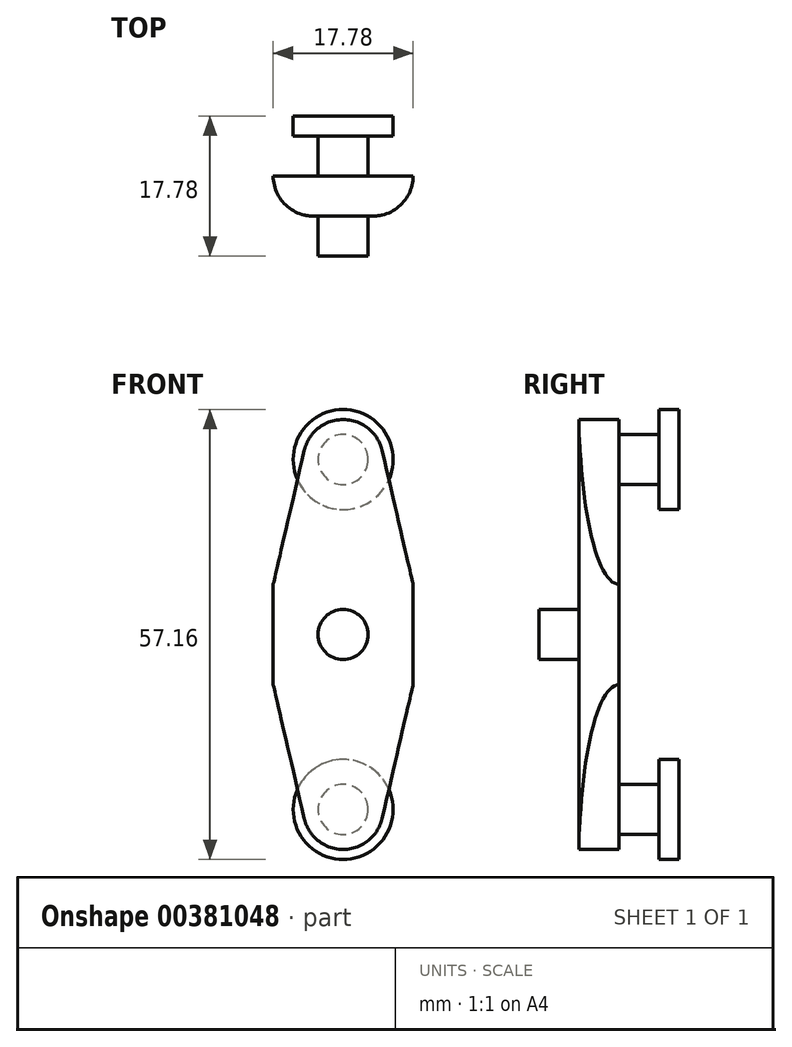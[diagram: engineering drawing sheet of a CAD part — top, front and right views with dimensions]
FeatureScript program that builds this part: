
annotation { "Feature Type Name" : "Feature", "Feature Type Description" : "" }
export const myFeature = defineFeature(function(context is Context, id is Id, definition is map)
    precondition{}
    {
        {
            var Q0;
            Q0=qCreatedBy(makeId("Front.planeOp"),FACE);
            var sketch = newSketch(context, id + "F0", { "sketchPlane" : qUnion([Q0])});
            skCircle(sketch, "E0", {"center": v(0, 22.23) * mm, "radius": 6.35 * mm});
            skSolve(sketch);
        }
        {
            var Q0;
            Q0 = qSketchRegion(id + "F0", true);
            extrude(context, id + "F1", {"entities" : qUnion([Q0]), "depth" : 2.54 * mm});
        }
        {
            var Q0;
            Q0=makeQuery(id+"F1.opExtrude","CAP_FACE",FACE,{"disambiguationData":[OSD([sQuery(id+"F0.wireOp",EDGE,"E0")])],"isStart":false});
            var sketch = newSketch(context, id + "F2", { "sketchPlane" : qUnion([Q0])});
            skCircle(sketch, "E1", {"center": v(0, 22.23) * mm, "radius": 3.18 * mm});
            skSolve(sketch);
        }
        {
            var Q0;
            Q0=makeQuery(id+"F2.imprint","IMPRINT",FACE,{"disambiguationData":[TD([[makeQuery(id+"F2.imprint","IMPRINT",EDGE,{"derivedFrom":sQuery(id+"F2.wireOp",EDGE,"E1")}),1.0]])]});
            extrude(context, id + "F3", {"entities" : qUnion([Q0]), "operationType" : NewBodyOperationType.ADD, "depth" : 5.08 * mm});
        }
        {
            var Q0;
            Q0=makeQuery(id+"F3.opExtrude","CAP_FACE",FACE,{"disambiguationData":[OSD([sQuery(id+"F2.wireOp",EDGE,"E1")])],"isStart":false});
            var sketch = newSketch(context, id + "F4", { "sketchPlane" : qUnion([Q0])});
            skCircle(sketch, "E2", {"center": v(0, 22.23) * mm, "radius": 5.08 * mm});
            skLineSegment(sketch, "E3.bottom", {"start": v(8.9, 6.35) * mm, "end": v(-8.9, 6.35) * mm});
            skLineSegment(sketch, "E3.top", {"start": v(8.9, -6.35) * mm, "end": v(-8.9, -6.35) * mm});
            skLineSegment(sketch, "E3.left", {"start": v(8.9, 6.35) * mm, "end": v(8.9, -6.35) * mm});
            skLineSegment(sketch, "E3.right", {"start": v(-8.9, 6.35) * mm, "end": v(-8.9, -6.35) * mm});
            skPoint(sketch, "E3.middle", {"position": v(0, 0) * mm});
            skLineSegment(sketch, "E4", {"start": v(8.9, 6.35) * mm, "end": v(4.95, 23.37) * mm});
            skLineSegment(sketch, "E5", {"start": v(-4.95, 23.37) * mm, "end": v(-8.89, 6.35) * mm});
            skSolve(sketch);
        }
        {
            var Q0;
            Q0=makeQuery(id+"F4.imprint","IMPRINT",FACE,{"disambiguationData":[TD([[makeQuery(id+"F4.imprint","IMPRINT",EDGE,{"derivedFrom":sQuery(id+"F4.wireOp",EDGE,"E3.bottom")}),-1.0]])]});
            var Q1;
            Q1=makeQuery(id+"F4.imprint","IMPRINT",FACE,{"disambiguationData":[TD([[makeQuery(id+"F4.imprint","IMPRINT",EDGE,{"derivedFrom":makeQuery(id+"F3.opExtrude","CAP_EDGE",EDGE,{"disambiguationData":[OSD([sQuery(id+"F2.wireOp",EDGE,"E1")])],"isStart":false})}),-1.0]])]});
            var Q2;
            Q2=makeQuery(id+"F4.imprint","IMPRINT",FACE,{"disambiguationData":[TD([[makeQuery(id+"F4.imprint","IMPRINT",EDGE,{"derivedFrom":makeQuery(id+"F3.opExtrude","CAP_EDGE",EDGE,{"disambiguationData":[OSD([sQuery(id+"F2.wireOp",EDGE,"E1")])],"isStart":false})}),1.0]])]});
            var Q3;
            Q3=makeQuery(id+"F4.imprint","IMPRINT",FACE,{"disambiguationData":[TD([[makeQuery(id+"F4.imprint","IMPRINT",EDGE,{"derivedFrom":sQuery(id+"F4.wireOp",EDGE,"E3.bottom")}),1.0]])]});
            extrude(context, id + "F5", {"entities" : qUnion([Q0, Q1, Q2, Q3]), "operationType" : NewBodyOperationType.ADD, "depth" : 5.08 * mm});
        }
        {
            var Q0;
            Q0=makeQuery(id+"F1.opExtrude","SWEPT_BODY",BODY,{"disambiguationData":[OSD([sQuery(id+"F0.wireOp",EDGE,"E0")])]});
            var Q1;
            Q1=qCreatedBy(makeId("Top.planeOp"),FACE);
            mirror(context, id + "F6", {"operationType" : NewBodyOperationType.ADD, "entities" : qUnion([Q0]), "mirrorPlane" : qUnion([Q1])});
        }
        {
            var Q0;
            Q0=makeQuery(id+"F5.opExtrude","CAP_EDGE",EDGE,{"disambiguationData":[OSD([sQuery(id+"F4.wireOp",EDGE,"E3.right")])],"isStart":false});
            var Q1;
            Q1=makeQuery(id+"F5.opExtrude","CAP_EDGE",EDGE,{"disambiguationData":[OSD([sQuery(id+"F4.wireOp",EDGE,"E3.left")])],"isStart":false});
            fillet(context, id + "F7", {"entities" : qUnion([Q0, Q1]), "radius" : 5.08 * mm, "tangentPropagation" : true, "allowEdgeOverflow" : false});
        }
        {
            var Q0;
            {var subQ0=makeQuery(id+"F5.opExtrude","CAP_FACE",FACE,{"disambiguationData":[OSD([sQuery(id+"F4.wireOp",EDGE,"E2"),sQuery(id+"F4.wireOp",EDGE,"E3.top"),sQuery(id+"F4.wireOp",EDGE,"E3.left"),sQuery(id+"F4.wireOp",EDGE,"E3.right"),sQuery(id+"F4.wireOp",EDGE,"E4"),sQuery(id+"F4.wireOp",EDGE,"E5")])],"isStart":false});Q0=makeQuery(id+"F6.boolean.opBoolean","MERGE",FACE,{"derivedFrom":[subQ0,makeQuery(id+"F6.opPattern","COPY",FACE,{"derivedFrom":subQ0,"instanceName":"1"})]});}
            var sketch = newSketch(context, id + "F8", { "sketchPlane" : qUnion([Q0])});
            skCircle(sketch, "E6", {"center": v(0, 0) * mm, "radius": 3.18 * mm});
            skSolve(sketch);
        }
        {
            var Q0;
            Q0=makeQuery(id+"F8.imprint","IMPRINT",FACE,{"disambiguationData":[TD([[makeQuery(id+"F8.imprint","IMPRINT",EDGE,{"derivedFrom":sQuery(id+"F8.wireOp",EDGE,"E6")}),1.0]])]});
            extrude(context, id + "F9", {"entities" : qUnion([Q0]), "operationType" : NewBodyOperationType.ADD, "depth" : 5.08 * mm});
        }
    });
